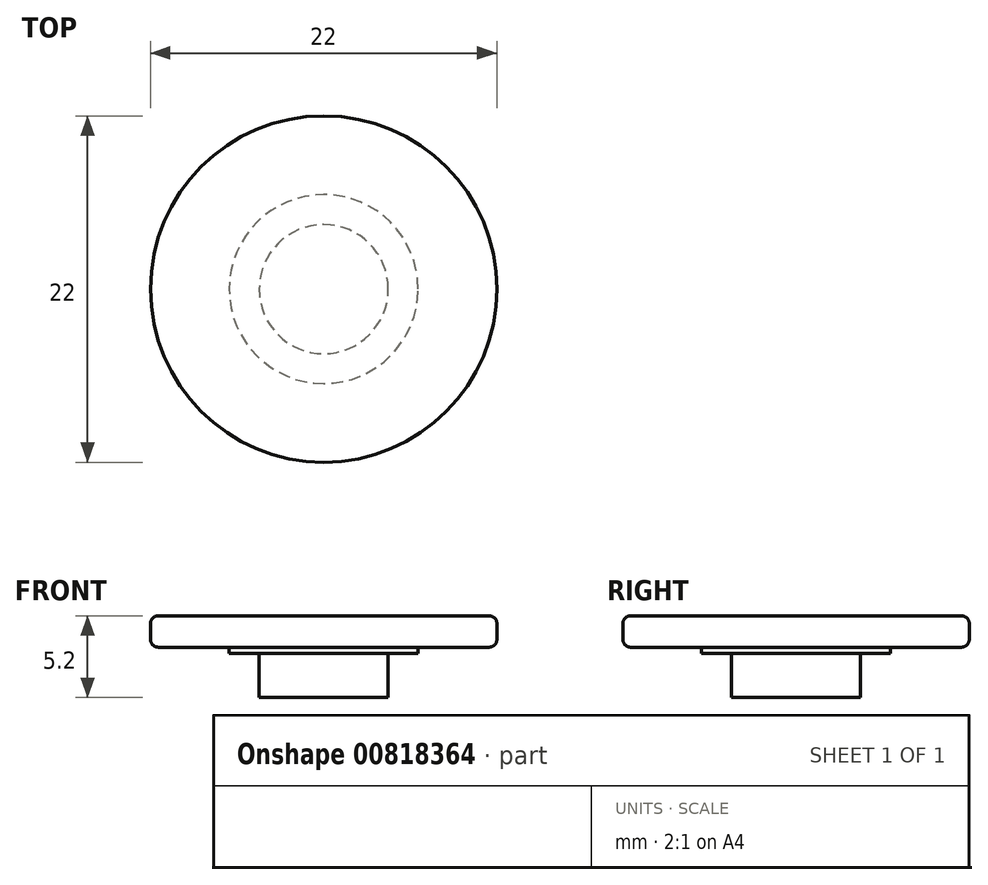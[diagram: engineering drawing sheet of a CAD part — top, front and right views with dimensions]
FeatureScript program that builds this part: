
annotation { "Feature Type Name" : "Feature", "Feature Type Description" : "" }
export const myFeature = defineFeature(function(context is Context, id is Id, definition is map)
    precondition{}
    {
        {
            var Q0;
            Q0=qCreatedBy(makeId("Front.planeOp"),FACE);
            var sketch = newSketch(context, id + "F0", { "sketchPlane" : qUnion([Q0])});
            skLineSegment(sketch, "E0", {"start": v(0, 0) * mm, "end": v(11, 0) * mm});
            skPoint(sketch, "E1.snap10", {"position": v(5.5, 0) * mm});
            skLineSegment(sketch, "E2.bottom", {"start": v(0, 0) * mm, "end": v(4.1, 0) * mm});
            skLineSegment(sketch, "E2.top", {"start": v(0, -3.2) * mm, "end": v(4.1, -3.2) * mm});
            skLineSegment(sketch, "E2.left", {"start": v(0, 0) * mm, "end": v(0, -3.2) * mm});
            skLineSegment(sketch, "E2.right", {"start": v(4.1, 0) * mm, "end": v(4.1, -3.2) * mm});
            skLineSegment(sketch, "E3.bottom", {"start": v(0, 0) * mm, "end": v(6, 0) * mm});
            skLineSegment(sketch, "E3.top", {"start": v(0, -0.4) * mm, "end": v(6, -0.4) * mm});
            skLineSegment(sketch, "E3.left", {"start": v(0, 0) * mm, "end": v(0, -0.4) * mm});
            skLineSegment(sketch, "E3.right", {"start": v(6, 0) * mm, "end": v(6, -0.4) * mm});
            skPoint(sketch, "E4", {"position": v(4.1, -0.4) * mm});
            skLineSegment(sketch, "E5", {"start": v(0, 0) * mm, "end": v(0, 2) * mm});
            skLineSegment(sketch, "E6", {"start": v(11, 2) * mm, "end": v(11, 0) * mm});
            skLineSegment(sketch, "E7", {"start": v(0, 2) * mm, "end": v(11, 2) * mm});
            skSolve(sketch);
        }
        {
            var Q0;
            Q0=qSketchRegion(id+"F0",true);
            var Q1;
            Q1=sQuery(id+"F0.wireOp",EDGE,"E5");
            revolve(context, id + "F1", {"surfaceOperationType" : NewSurfaceOperationType.NEW, "entities" : qUnion([Q0]), "axis" : qUnion([Q1]), "revolveType" : RevolveType.FULL});
        }
        {
            var Q0;
            Q0=makeQuery(id+"F1.opRevolve","SWEPT_EDGE",EDGE,{"disambiguationData":[OSD([sQuery(id+"F0.wireOp",EDGE,"9hwaFN4s-kBqj-5SZZ-FVYH-1m46pSyMPwgE"),sQuery(id+"F0.wireOp",EDGE,"w00q5z8J-IB3I-pAUQ-ONzX-yISjesTEle08")])]});
            var Q1;
            Q1=makeQuery(id+"F1.opRevolve","SWEPT_EDGE",EDGE,{"disambiguationData":[OSD([sQuery(id+"F0.wireOp",EDGE,"bjdI8zht-WpHH-Crd8-jyY7-Y7Y6zSUyLd9y"),sQuery(id+"F0.wireOp",EDGE,"E6")])]});
            fillet(context, id + "F2", {"entities" : qUnion([Q0, Q1]), "radius" : 0.5 * mm, "tangentPropagation" : true, "allowEdgeOverflow" : false});
        }
    });
